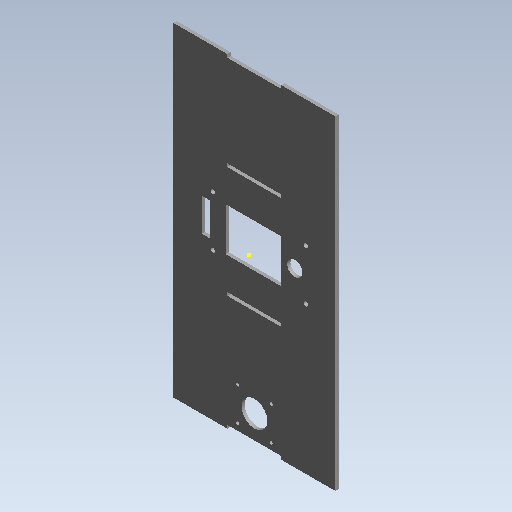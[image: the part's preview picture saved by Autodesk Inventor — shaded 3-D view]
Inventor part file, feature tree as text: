
AUTODESK INVENTOR PART (.ipt)
format: ipt  version: 2020 (Build 240168000, 168)  size: 208,896 bytes
history: native  units: mm (DEFAULTED — no unit token found)
features: sketch x20, extrude x16
ambient origin geometry x8: Origin, YZ Plane, XZ Plane, XY Plane, X Axis, Y Axis, Z Axis, Center Point
bodies: Solid1 (feature_tree)
feature tree (36):
  extrude  "Extrusion1"  Depth=50.0mm
  sketch  "3D Sketch1"
  extrude  "Extrusion2"  Depth=3.0mm TaperAngle=0.0deg
  extrude  "Extrusion3"  Depth=3.0mm TaperAngle=0.0deg
  extrude  "Extrusion4"  Depth=3.0mm TaperAngle=0.0deg
  extrude  "Extrusion5"  Depth=3.0mm TaperAngle=0.0deg
  extrude  "Extrusion6"  Depth=10.0mm
  extrude  "Extrusion7"  Depth=31.999867mm
  extrude  "Extrusion8"  Depth=3.0mm TaperAngle=0.0deg
  sketch  "Sketch9"  dims[d114=3.0mm d115=0.0mm d116=3.0mm d117=0.0mm]
  sketch  "Sketch10"  dims[d118=3.0mm d119=0.0mm d133=35.75mm d134=0.0mm]
  extrude  "Extrusion9"  Depth=3.0mm TaperAngle=0.0deg
  extrude  "Extrusion10"  Depth=35.75mm TaperAngle=0.0deg
  extrude  "Extrusion11"  [1 undecoded]
  extrude  "Extrusion12"  [1 undecoded]
  extrude  "Extrusion13"  [1 undecoded]
  extrude  "Extrusion14"  [1 undecoded]
  extrude  "Extrusion15"  [1 undecoded]
  extrude  "Extrusion16"  [1 undecoded]
  sketch  "Sketch19"
  sketch  "Sketch1"  dims[d2=3.0mm d3=0.0mm d9=50.0mm]
  sketch  "Sketch2"  dims[d14=3.0mm d15=0.0mm d21=3.0mm d22=0.0mm]
  sketch  "Sketch3"  dims[d25=3.0mm d26=0.0mm d31=3.0mm d32=0.0mm]
  sketch  "Sketch4"  dims[d37=3.0mm d38=0.0mm d45=3.0mm d46=0.0mm]
  sketch  "Sketch5"  dims[d58=3.0mm d59=0.0mm d102=30.0mm d103=0.0mm]
  sketch  "Sketch6"  dims[d104=10.0mm d105=0.0mm d107=15.0mm]
  sketch  "Sketch7"  dims[d108=32.056514mm d109=31.999867mm]
  sketch  "Sketch8"  dims[d110=3.0mm d111=0.0mm d112=3.0mm d113=0.0mm]
  sketch  "Sketch11"
  sketch  "Sketch12"
  sketch  "Sketch13"
  sketch  "Sketch14"
  sketch  "Sketch15"
  sketch  "Sketch16"
  sketch  "Sketch17"
  sketch  "Sketch18"
note: 6 required parameter values undecoded (feature->parameter linkage not recoverable at this tier; creation-order binding heuristic only, values carry confidence <= 0.55)
